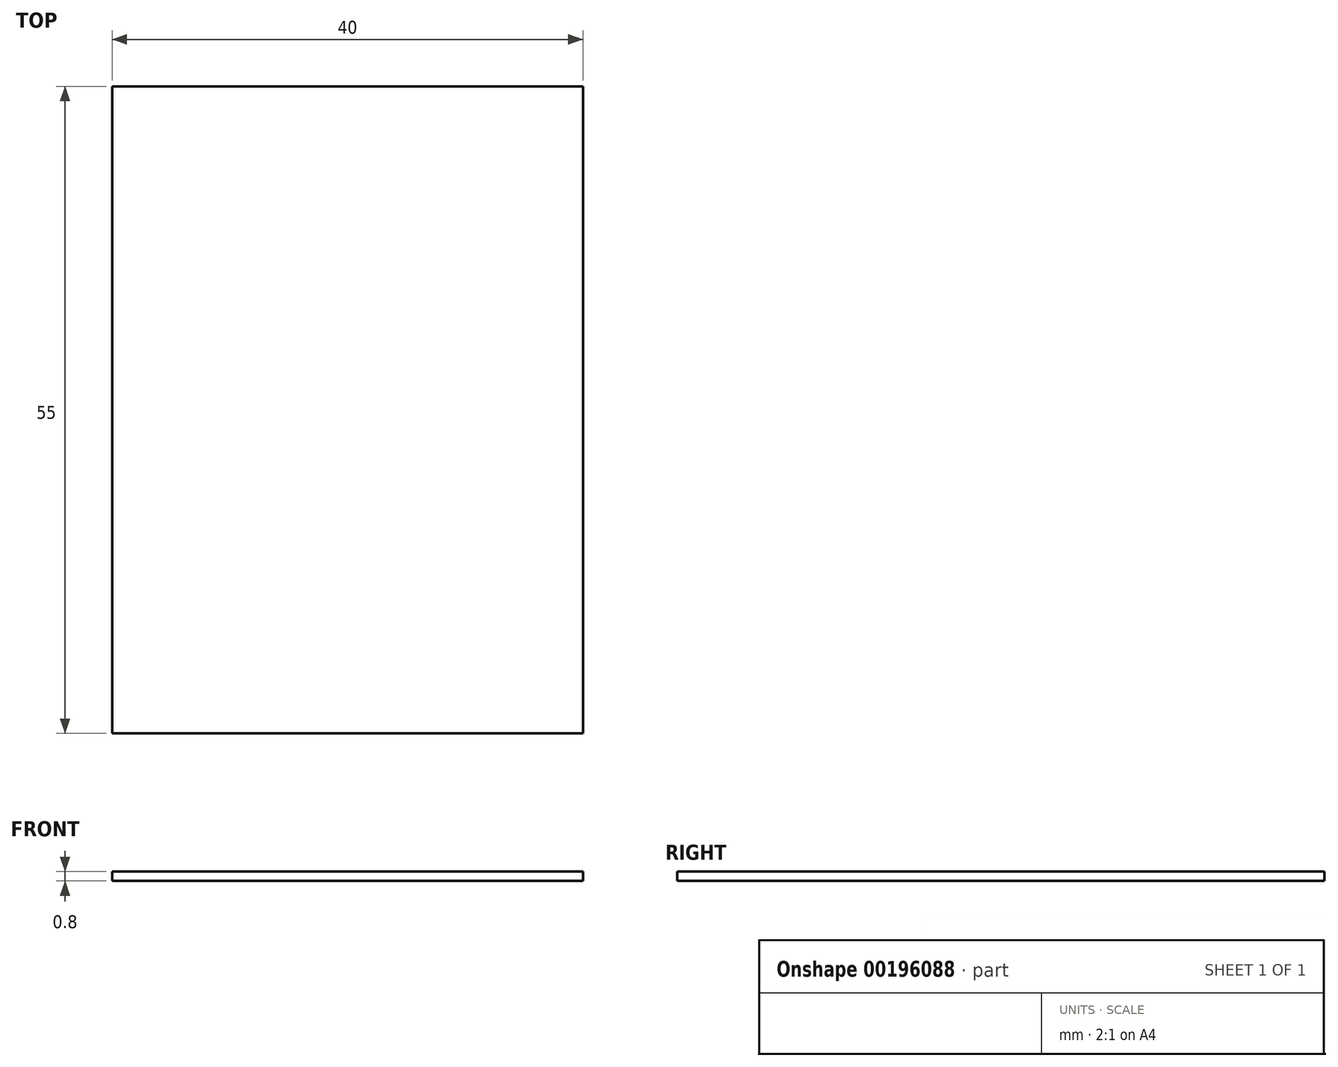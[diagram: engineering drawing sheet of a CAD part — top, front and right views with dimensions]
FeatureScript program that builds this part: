
annotation { "Feature Type Name" : "Feature", "Feature Type Description" : "" }
export const myFeature = defineFeature(function(context is Context, id is Id, definition is map)
    precondition{}
    {
        {
            var Q0;
            Q0=qCreatedBy(makeId("Top.planeOp"),FACE);
            var sketch = newSketch(context, id + "F0", { "sketchPlane" : qUnion([Q0])});
            skLineSegment(sketch, "E0.bottom", {"start": v(0, 0) * mm, "end": v(-40, 0) * mm});
            skLineSegment(sketch, "E0.top", {"start": v(0, 55) * mm, "end": v(-40, 55) * mm});
            skLineSegment(sketch, "E0.left", {"start": v(0, 0) * mm, "end": v(0, 55) * mm});
            skLineSegment(sketch, "E0.right", {"start": v(-40, 0) * mm, "end": v(-40, 55) * mm});
            skLineSegment(sketch, "E1", {"start": v(-40, 55) * mm, "end": v(-40, 110) * mm});
            skLineSegment(sketch, "E2", {"start": v(-40, 110) * mm, "end": v(0, 110) * mm});
            skLineSegment(sketch, "E3", {"start": v(0, 110) * mm, "end": v(0, 55) * mm});
            skLineSegment(sketch, "E4", {"start": v(-40, 110) * mm, "end": v(-40, 165) * mm});
            skLineSegment(sketch, "E5", {"start": v(-40, 165) * mm, "end": v(0, 165) * mm});
            skLineSegment(sketch, "E6", {"start": v(0, 165) * mm, "end": v(0, 110) * mm});
            skLineSegment(sketch, "E7", {"start": v(-40, 165) * mm, "end": v(-40, 220) * mm});
            skLineSegment(sketch, "E8", {"start": v(-40, 220) * mm, "end": v(0, 220) * mm});
            skLineSegment(sketch, "E9", {"start": v(0, 220) * mm, "end": v(0, 165) * mm});
            skLineSegment(sketch, "E10", {"start": v(0, 55) * mm, "end": v(40, 55) * mm});
            skLineSegment(sketch, "E11", {"start": v(40, 55) * mm, "end": v(40, 0) * mm});
            skLineSegment(sketch, "E12", {"start": v(40, 0) * mm, "end": v(0, 0) * mm});
            skLineSegment(sketch, "E13", {"start": v(40, 55) * mm, "end": v(120, 55) * mm});
            skLineSegment(sketch, "E14", {"start": v(120, 55) * mm, "end": v(120, 0) * mm});
            skLineSegment(sketch, "E15", {"start": v(120, 0) * mm, "end": v(40, 0) * mm});
            skLineSegment(sketch, "E16", {"start": v(120, 55) * mm, "end": v(200, 55) * mm});
            skLineSegment(sketch, "E17", {"start": v(200, 55) * mm, "end": v(200, 0) * mm});
            skLineSegment(sketch, "E18", {"start": v(200, 0) * mm, "end": v(120, 0) * mm});
            skLineSegment(sketch, "E19", {"start": v(0, 110) * mm, "end": v(40, 110) * mm});
            skLineSegment(sketch, "E20", {"start": v(40, 110) * mm, "end": v(40, 55) * mm});
            skLineSegment(sketch, "E21", {"start": v(0, 220) * mm, "end": v(40, 220) * mm});
            skLineSegment(sketch, "E22", {"start": v(40, 220) * mm, "end": v(40, 110) * mm});
            skLineSegment(sketch, "E23", {"start": v(40, 110) * mm, "end": v(120, 110) * mm});
            skLineSegment(sketch, "E24", {"start": v(120, 110) * mm, "end": v(120, 55) * mm});
            skLineSegment(sketch, "E25.bottom", {"start": v(200, 0) * mm, "end": v(280, 0) * mm});
            skLineSegment(sketch, "E25.top", {"start": v(200, 55) * mm, "end": v(280, 55) * mm});
            skLineSegment(sketch, "E25.left", {"start": v(200, 0) * mm, "end": v(200, 55) * mm});
            skLineSegment(sketch, "E25.right", {"start": v(280, 0) * mm, "end": v(280, 55) * mm});
            skLineSegment(sketch, "E26.top", {"start": v(120, 110) * mm, "end": v(200, 110) * mm});
            skLineSegment(sketch, "E26.left", {"start": v(120, 55) * mm, "end": v(120, 110) * mm});
            skLineSegment(sketch, "E26.right", {"start": v(200, 55) * mm, "end": v(200, 110) * mm});
            skLineSegment(sketch, "E27.top", {"start": v(40, 165) * mm, "end": v(120, 165) * mm});
            skLineSegment(sketch, "E27.left", {"start": v(40, 110) * mm, "end": v(40, 165) * mm});
            skLineSegment(sketch, "E27.right", {"start": v(120, 110) * mm, "end": v(120, 165) * mm});
            skLineSegment(sketch, "E28.top", {"start": v(40, 220) * mm, "end": v(120, 220) * mm});
            skLineSegment(sketch, "E28.left", {"start": v(40, 165) * mm, "end": v(40, 220) * mm});
            skLineSegment(sketch, "E28.right", {"start": v(120, 165) * mm, "end": v(120, 220) * mm});
            skLineSegment(sketch, "E29.top", {"start": v(120, 165) * mm, "end": v(200, 165) * mm});
            skLineSegment(sketch, "E29.right", {"start": v(200, 110) * mm, "end": v(200, 165) * mm});
            skLineSegment(sketch, "E30.top", {"start": v(120, 220) * mm, "end": v(200, 220) * mm});
            skLineSegment(sketch, "E30.right", {"start": v(200, 165) * mm, "end": v(200, 220) * mm});
            skLineSegment(sketch, "E31.top", {"start": v(200, 110) * mm, "end": v(280, 110) * mm});
            skLineSegment(sketch, "E31.right", {"start": v(280, 55) * mm, "end": v(280, 110) * mm});
            skLineSegment(sketch, "E32.top", {"start": v(200, 165) * mm, "end": v(280, 165) * mm});
            skLineSegment(sketch, "E32.right", {"start": v(280, 110) * mm, "end": v(280, 165) * mm});
            skLineSegment(sketch, "E33.top", {"start": v(200, 220) * mm, "end": v(280, 220) * mm});
            skLineSegment(sketch, "E33.right", {"start": v(280, 165) * mm, "end": v(280, 220) * mm});
            skSolve(sketch);
        }
        {
            var Q0;
            Q0=makeQuery(id+"F0.imprint","IMPRINT",FACE,{"disambiguationData":[TD([[makeQuery(id+"F0.imprint","IMPRINT",EDGE,{"derivedFrom":sQuery(id+"F0.wireOp",EDGE,"E0.bottom")}),-1.0]])]});
            extrude(context, id + "F1", {"entities" : qUnion([Q0]), "depth" : 0.8 * mm, "offsetDistance" : 25 * mm});
        }
    });
